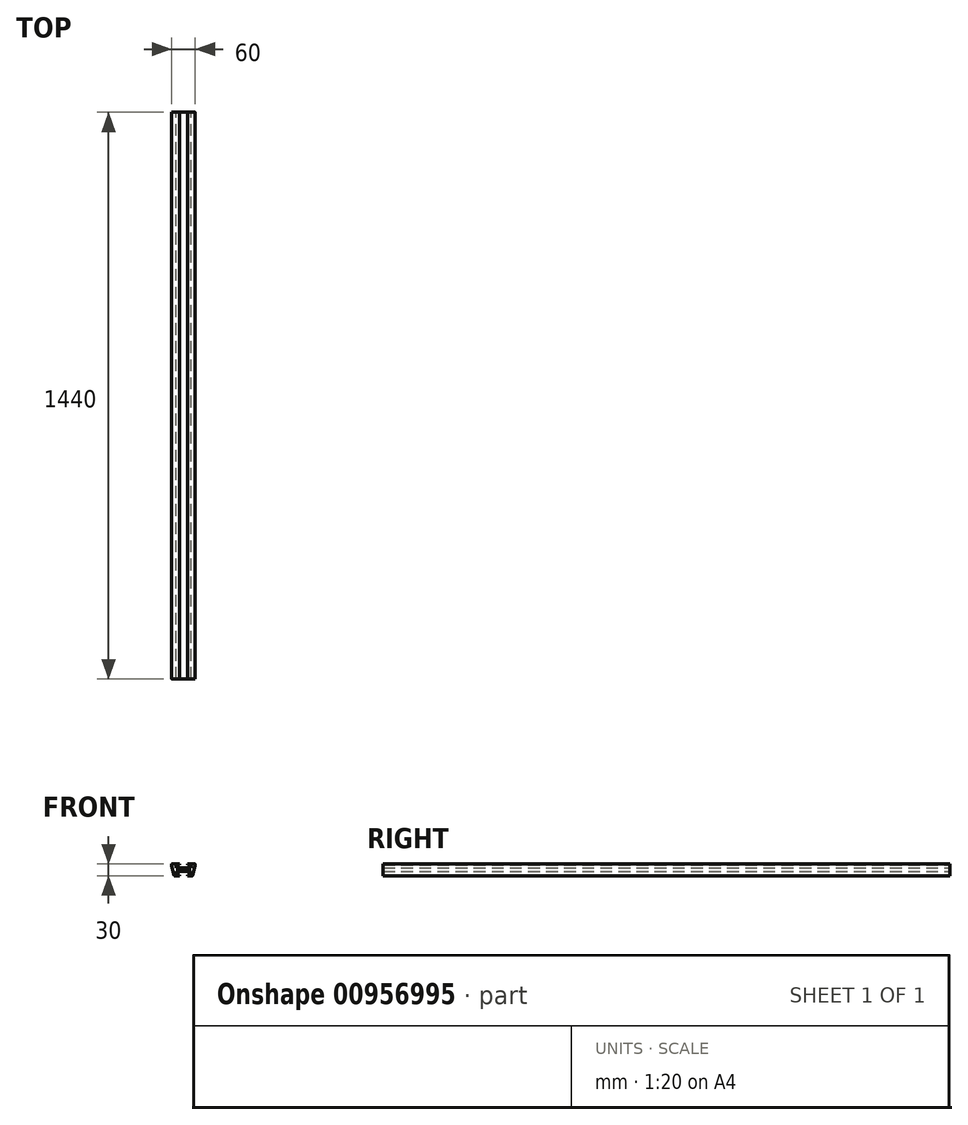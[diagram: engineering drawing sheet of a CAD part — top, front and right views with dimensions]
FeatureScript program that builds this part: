
annotation { "Feature Type Name" : "Feature", "Feature Type Description" : "" }
export const myFeature = defineFeature(function(context is Context, id is Id, definition is map)
    precondition{}
    {
        {
            var Q0;
            Q0=qCreatedBy(makeId("Front.planeOp"),FACE);
            var sketch = newSketch(context, id + "F0", { "sketchPlane" : qUnion([Q0])});
            skLineSegment(sketch, "E0.bottom", {"start": v(29.5, 15) * mm, "end": v(10, 15) * mm});
            skLineSegment(sketch, "E0.top", {"start": v(23.05, -15) * mm, "end": v(10, -15) * mm});
            skLineSegment(sketch, "E0.left", {"start": v(30, 14.5) * mm, "end": v(30, 9.54) * mm});
            skLineSegment(sketch, "E0.right", {"start": v(-30, 14.5) * mm, "end": v(-30, 9.54) * mm});
            skPoint(sketch, "E0.middle", {"position": v(0, 0) * mm});
            skLineSegment(sketch, "E1", {"start": v(-29.99, 9.46) * mm, "end": v(-23.53, -14.63) * mm});
            skLineSegment(sketch, "E2.MirrorCS", {"start": v(29.99, 9.46) * mm, "end": v(23.53, -14.63) * mm});
            skPoint(sketch, "E3.orphan", {"position": v(-30, -15) * mm});
            skPoint(sketch, "E4.orphan", {"position": v(30, -15) * mm});
            skLineSegment(sketch, "E5", {"start": v(-10, 15) * mm, "end": v(-10, 12.5) * mm});
            skLineSegment(sketch, "E6", {"start": v(-10, 12.5) * mm, "end": v(-19, 12.5) * mm});
            skLineSegment(sketch, "E7", {"start": v(-19, 12.5) * mm, "end": v(-19, 4.5) * mm});
            skLineSegment(sketch, "E8", {"start": v(-19, 4.5) * mm, "end": v(0, 4.5) * mm});
            skLineSegment(sketch, "E9.MirrorCS", {"start": v(10, 15) * mm, "end": v(10, 12.5) * mm});
            skLineSegment(sketch, "E10.MirrorCS", {"start": v(10, 12.5) * mm, "end": v(19, 12.5) * mm});
            skLineSegment(sketch, "E11.MirrorCS", {"start": v(19, 12.5) * mm, "end": v(19, 4.5) * mm});
            skLineSegment(sketch, "E12.MirrorCS", {"start": v(19, 4.5) * mm, "end": v(0, 4.5) * mm});
            skLineSegment(sketch, "E13.MirrorCS", {"start": v(-10, -12.5) * mm, "end": v(-19, -12.5) * mm});
            skLineSegment(sketch, "E14.MirrorCS", {"start": v(-10, -15) * mm, "end": v(-10, -12.5) * mm});
            skLineSegment(sketch, "E15.MirrorCS", {"start": v(19, -4.5) * mm, "end": v(0, -4.5) * mm});
            skLineSegment(sketch, "E16.MirrorCS", {"start": v(-19, -4.5) * mm, "end": v(0, -4.5) * mm});
            skLineSegment(sketch, "E17.MirrorCS", {"start": v(19, -12.5) * mm, "end": v(19, -4.5) * mm});
            skLineSegment(sketch, "E18.MirrorCS", {"start": v(10, -12.5) * mm, "end": v(19, -12.5) * mm});
            skLineSegment(sketch, "E19.MirrorCS", {"start": v(10, -15) * mm, "end": v(10, -12.5) * mm});
            skLineSegment(sketch, "E20.MirrorCS", {"start": v(-19, -12.5) * mm, "end": v(-19, -4.5) * mm});
            skLineSegment(sketch, "E21.trimOffspring", {"start": v(-10, 15) * mm, "end": v(-29.5, 15) * mm});
            skLineSegment(sketch, "E22.trimOffspring", {"start": v(-10, -15) * mm, "end": v(-23.05, -15) * mm});
            skPoint(sketch, "E23.visualSharp", {"position": v(-30, 15) * mm});
            skArc(sketch, "E23.filletArc", {"start": v(-29.5, 15) * mm, "mid": v(-29.85, 14.85) * mm, "end": v(-30, 14.5) * mm});
            skPoint(sketch, "E24.visualSharp", {"position": v(30, 15) * mm});
            skArc(sketch, "E24.filletArc", {"start": v(30, 14.5) * mm, "mid": v(29.85, 14.85) * mm, "end": v(29.5, 15) * mm});
            skPoint(sketch, "E25.visualSharp", {"position": v(-23.44, -15) * mm});
            skArc(sketch, "E25.filletArc", {"start": v(-23.53, -14.63) * mm, "mid": v(-23.36, -14.9) * mm, "end": v(-23.05, -15) * mm});
            skPoint(sketch, "E26.visualSharp", {"position": v(23.44, -15) * mm});
            skArc(sketch, "E26.filletArc", {"start": v(23.05, -15) * mm, "mid": v(23.36, -14.9) * mm, "end": v(23.53, -14.63) * mm});
            skPoint(sketch, "E27.visualSharp", {"position": v(-30, 9.5) * mm});
            skArc(sketch, "E27.filletArc", {"start": v(-30, 9.54) * mm, "mid": v(-30, 9.5) * mm, "end": v(-29.99, 9.46) * mm});
            skPoint(sketch, "E28.visualSharp", {"position": v(30, 9.5) * mm});
            skArc(sketch, "E28.filletArc", {"start": v(29.99, 9.46) * mm, "mid": v(30, 9.5) * mm, "end": v(30, 9.54) * mm});
            skSolve(sketch);
        }
        {
            var Q0;
            Q0=makeQuery(id+"F0.imprint","IMPRINT",FACE,{"disambiguationData":[TD([[makeQuery(id+"F0.imprint","IMPRINT",EDGE,{"derivedFrom":sQuery(id+"F0.wireOp",EDGE,"E0.bottom")}),1.0]])]});
            extrude(context, id + "F1", {"entities" : qUnion([Q0]), "endBound" : BoundingType.SYMMETRIC, "depth" : 1440 * mm, "offsetDistance" : 25 * mm});
        }
    });
